# Revit family: ITK_Комплект проводов заземления
name_source: partatom
category: Обобщенные модели
units: mm (PartAtom-declared; Revit-internal decimal feet)

## family parameters
Всегда вертикально = Да
Может служить основой для арматурных стержней = Нет
На основе рабочей плоскости = Нет
Общий = Нет
При загрузке вырезать с полостями = Нет
Размер круглого соединителя = Использовать диаметр
Тип детали = Нормальный
Точка расчета площади = Нет

## types (1)
- ER12-6568
    ADSK_URL страницы изделия = https://www.itk-group.ru
    ADSK_Версия Revit = 2019
    ADSK_Версия семейства = 1.0
    ADSK_Группирование = I. ЩИТЫ И ПУЛЬТЫ
    ADSK_Единица измерения = компл
    ADSK_Завод-изготовитель = IEK
    ADSK_Код изделия = ER12-6568
    ADSK_Масса = 0.21
    ADSK_Материал наименование = Медь без покрытия
    ADSK_Наименование = ITK Комплект проводов заземления 50 cм - 6шт; 80 cм - 3шт
    IEK_URL = https://www.itk-group.ru
    IEK_Описание = Совместимы со всеми 19" шкафами и стойками ITK.
Удобны в монтаже и эксплуатации.
Винты имеют резьбу М6.
Соответствие российским и международным стандартам.
Поставляются в полиэтиленовом пакете.
    IEK_Цена за единицу = 665.03
    KSI_CMa_Строительные материалы = 10.2.01.03
    KSI_CPr_Строительные изделия = 01.7.15.04
    URL = https://www.iek.ru
    Изготовитель = ITK
